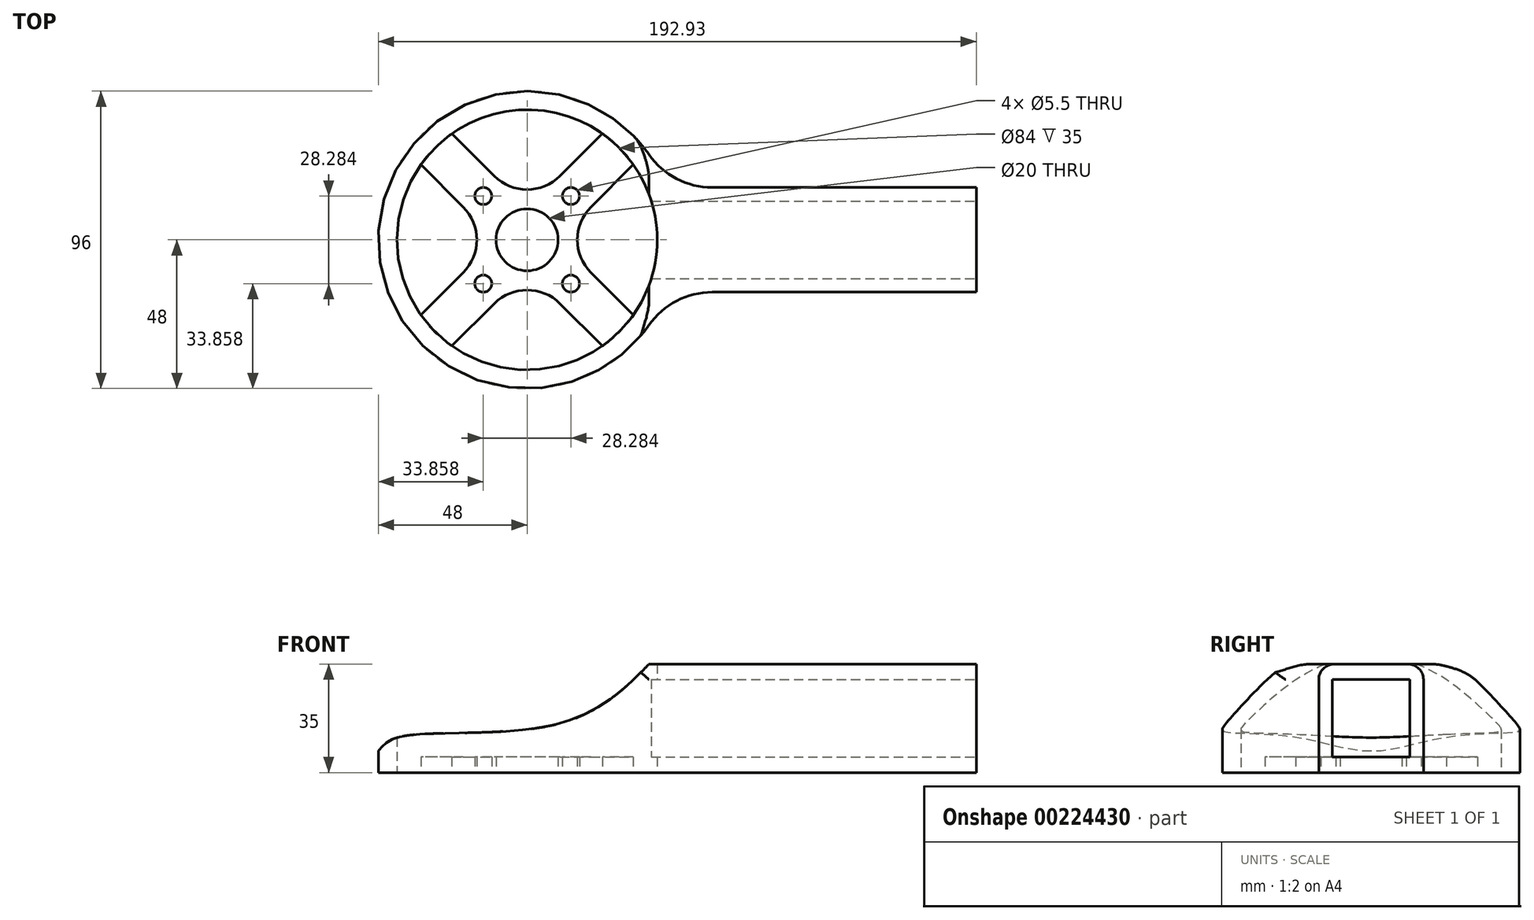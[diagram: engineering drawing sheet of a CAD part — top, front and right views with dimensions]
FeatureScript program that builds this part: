
annotation { "Feature Type Name" : "Feature", "Feature Type Description" : "" }
export const myFeature = defineFeature(function(context is Context, id is Id, definition is map)
    precondition{}
    {
        {
            var Q0;
            Q0=qCreatedBy(makeId("Top.planeOp"),FACE);
            var sketch = newSketch(context, id + "F0", { "sketchPlane" : qUnion([Q0])});
            skArc(sketch, "E0", {"start": v(39.3, 27.55) * mm, "mid": v(-48, 0) * mm, "end": v(39.3, -27.55) * mm});
            skCircle(sketch, "E1", {"center": v(0, 0) * mm, "radius": 20 * mm, "construction": true});
            skCircle(sketch, "E2", {"center": v(0, 0) * mm, "radius": 42 * mm});
            skLineSegment(sketch, "E3", {"start": v(59.78, 16.9) * mm, "end": v(144.93, 16.9) * mm});
            skLineSegment(sketch, "E4", {"start": v(59.78, -16.9) * mm, "end": v(144.93, -16.9) * mm});
            skCircle(sketch, "E5", {"center": v(0, 0) * mm, "radius": 10 * mm});
            skCircle(sketch, "E6", {"center": v(-14.14, 14.14) * mm, "radius": 2.75 * mm});
            skCircle(sketch, "E7", {"center": v(14.14, 14.14) * mm, "radius": 2.75 * mm});
            skCircle(sketch, "E8", {"center": v(14.14, -14.14) * mm, "radius": 2.75 * mm});
            skCircle(sketch, "E9", {"center": v(-14.14, -14.14) * mm, "radius": 2.75 * mm});
            skLineSegment(sketch, "E10", {"start": v(-14.14, 14.14) * mm, "end": v(-14.14, -14.14) * mm, "construction": true});
            skLineSegment(sketch, "E11", {"start": v(-14.14, -14.14) * mm, "end": v(14.14, -14.14) * mm, "construction": true});
            skLineSegment(sketch, "E12", {"start": v(-24.27, 34.27) * mm, "end": v(-10.6, 20.6) * mm});
            skLineSegment(sketch, "E13", {"start": v(10.6, 20.6) * mm, "end": v(24.27, 34.27) * mm});
            skLineSegment(sketch, "E14", {"start": v(34.27, 24.27) * mm, "end": v(20.6, 10.6) * mm});
            skLineSegment(sketch, "E15", {"start": v(20.6, -10.6) * mm, "end": v(34.27, -24.27) * mm});
            skLineSegment(sketch, "E16", {"start": v(24.27, -34.27) * mm, "end": v(10.6, -20.6) * mm});
            skLineSegment(sketch, "E17", {"start": v(-10.6, -20.6) * mm, "end": v(-24.27, -34.27) * mm});
            skLineSegment(sketch, "E18", {"start": v(-34.27, -24.27) * mm, "end": v(-20.6, -10.6) * mm});
            skLineSegment(sketch, "E19", {"start": v(-20.6, 10.6) * mm, "end": v(-34.27, 24.27) * mm});
            skPoint(sketch, "E20.visualSharp", {"position": v(0, 10) * mm});
            skArc(sketch, "E20.filletArc", {"start": v(-10.6, 20.6) * mm, "mid": v(0, 16.21) * mm, "end": v(10.6, 20.6) * mm});
            skPoint(sketch, "E21.visualSharp", {"position": v(10, 0) * mm});
            skArc(sketch, "E21.filletArc", {"start": v(20.6, 10.6) * mm, "mid": v(16.21, 0) * mm, "end": v(20.6, -10.6) * mm});
            skPoint(sketch, "E22.visualSharp", {"position": v(0, -10) * mm});
            skArc(sketch, "E22.filletArc", {"start": v(10.6, -20.6) * mm, "mid": v(0, -16.21) * mm, "end": v(-10.6, -20.6) * mm});
            skPoint(sketch, "E23.visualSharp", {"position": v(-10, 0) * mm});
            skArc(sketch, "E23.filletArc", {"start": v(-20.6, -10.6) * mm, "mid": v(-16.21, 0) * mm, "end": v(-20.6, 10.6) * mm});
            skLineSegment(sketch, "E24", {"start": v(144.93, 16.9) * mm, "end": v(144.93, -16.9) * mm});
            skPoint(sketch, "E25.visualSharp", {"position": v(44.93, 16.9) * mm});
            skArc(sketch, "E25.filletArc", {"start": v(39.3, 27.55) * mm, "mid": v(48.24, 19.71) * mm, "end": v(59.78, 16.9) * mm});
            skPoint(sketch, "E26.visualSharp", {"position": v(44.93, -16.9) * mm});
            skArc(sketch, "E26.filletArc", {"start": v(59.78, -16.9) * mm, "mid": v(48.24, -19.71) * mm, "end": v(39.3, -27.55) * mm});
            skSolve(sketch);
        }
        {
            var Q0;
            Q0=makeQuery(id+"F0.imprint","IMPRINT",FACE,{"disambiguationData":[TD([[makeQuery(id+"F0.imprint","IMPRINT",EDGE,{"derivedFrom":sQuery(id+"F0.wireOp",EDGE,"E5")}),-1.0]])]});
            var Q1;
            {var subQ4=sQuery(id+"F0.wireOp",EDGE,"E0");var subQ5=makeQuery(id+"F0.imprint","IMPRINT",VERTEX,{"disambiguationData":[OD(0.0)],"derivedFrom":subQ4});Q1=makeQuery(id+"F0.imprint","IMPRINT",FACE,{"disambiguationData":[TD([[makeQuery(id+"F0.imprint","IMPRINT",EDGE,{"disambiguationData":[TD([[subQ5,-1.0]])],"derivedFrom":subQ4}),1.0]])]});}
            extrude(context, id + "F1", {"entities" : qUnion([Q0, Q1]), "depth" : 5 * mm});
        }
        {
            var Q0;
            Q0=makeQuery(id+"F0.imprint","IMPRINT",FACE,{"disambiguationData":[TD([[makeQuery(id+"F0.imprint","IMPRINT",EDGE,{"derivedFrom":sQuery(id+"F0.wireOp",EDGE,"E0")}),1.0]])]});
            extrude(context, id + "F2", {"entities" : qUnion([Q0]), "operationType" : NewBodyOperationType.ADD, "depth" : 35 * mm});
        }
        {
            var Q0;
            Q0=makeQuery(id+"F2.opExtrude","SWEPT_FACE",FACE,{"disambiguationData":[OSD([sQuery(id+"F0.wireOp",EDGE,"E24")])]});
            var sketch = newSketch(context, id + "F3", { "sketchPlane" : qUnion([Q0])});
            skLineSegment(sketch, "E27.bottom", {"start": v(12.5, 30) * mm, "end": v(-12.5, 30) * mm});
            skLineSegment(sketch, "E27.top", {"start": v(12.5, 5) * mm, "end": v(-12.5, 5) * mm});
            skLineSegment(sketch, "E27.left", {"start": v(12.5, 30) * mm, "end": v(12.5, 5) * mm});
            skLineSegment(sketch, "E27.right", {"start": v(-12.5, 30) * mm, "end": v(-12.5, 5) * mm});
            skPoint(sketch, "E27.middle", {"position": v(0, 17.5) * mm});
            skPoint(sketch, "E27.middle.positionSnap0", {"position": v(16.9, 17.5) * mm});
            skPoint(sketch, "E27.centerSnap0", {"position": v(16.9, 17.5) * mm});
            skSolve(sketch);
        }
        {
            var Q0;
            Q0=makeQuery(id+"F3.imprint","IMPRINT",FACE,{"disambiguationData":[TD([[makeQuery(id+"F3.imprint","IMPRINT",EDGE,{"derivedFrom":sQuery(id+"F3.wireOp",EDGE,"E27.bottom")}),1.0]])]});
            extrude(context, id + "F4", {"entities" : qUnion([Q0]), "operationType" : NewBodyOperationType.REMOVE, "oppositeDirection" : true, "depth" : 120 * mm});
        }
        {
            var Q0;
            Q0=qCreatedBy(makeId("Front.planeOp"),FACE);
            var sketch = newSketch(context, id + "F5", { "sketchPlane" : qUnion([Q0])});
            skFitSpline(sketch, "E28", {"points": [v(39.31, 35) * mm, v(8.45, 15.36) * mm, v(-41.36, 11.48) * mm, v(-48, 6.91) * mm], "startDerivative": vector(-65.63, -68.43) * mm, "endDerivative": vector(-24.96, -33.25) * mm});
            skLineSegment(sketch, "E29", {"start": v(39.31, 35) * mm, "end": v(-49.96, 58.38) * mm});
            skLineSegment(sketch, "E30", {"start": v(-49.96, 58.38) * mm, "end": v(-62.52, 10.41) * mm});
            skLineSegment(sketch, "E31", {"start": v(-62.52, 10.41) * mm, "end": v(-48, 6.91) * mm});
            skSolve(sketch);
        }
        {
            var Q0;
            Q0 = qSketchRegion(id + "F5", true);
            extrude(context, id + "F6", {"entities" : qUnion([Q0]), "operationType" : NewBodyOperationType.REMOVE, "endBound" : BoundingType.SYMMETRIC, "depth" : 100 * mm});
        }
        {
            var Q0;
            Q0=makeQuery(id+"F2.opExtrude","CAP_EDGE",EDGE,{"disambiguationData":[OSD([sQuery(id+"F0.wireOp",EDGE,"E4")])],"isStart":false});
            var Q1;
            Q1=makeQuery(id+"F2.opExtrude","CAP_EDGE",EDGE,{"disambiguationData":[OSD([sQuery(id+"F0.wireOp",EDGE,"E3")])],"isStart":false});
            fillet(context, id + "F7", {"entities" : qUnion([Q0, Q1]), "radius" : 5 * mm, "tangentPropagation" : true, "allowEdgeOverflow" : false});
        }
    });
